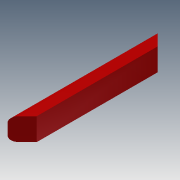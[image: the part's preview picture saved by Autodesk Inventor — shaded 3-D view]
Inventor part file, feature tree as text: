
AUTODESK INVENTOR PART (.ipt)
format: ipt  version: 2014 (Build 180170000, 170)  size: 93,184 bytes
history: native  units: in
note: dims shown in document units (in); Inventor stores cm internally (conversion verified against a paired STEP export)
features: extrude x2, sketch x2
ambient origin geometry x8: Origin, YZ Plane, XZ Plane, XY Plane, X Axis, Y Axis, Z Axis, Center Point
bodies: Solid1 (feature_tree)
feature tree (4):
  extrude  "Extrusion1"  Depth=5.0in
  extrude  "Extrusion2"  Depth=5.0in
  sketch  "Sketch1"  dims[d0=0.75in d1=5.0in]
  sketch  "Sketch2"  dims[d2=2.5in d3=2.5in d4=1.25in d5=33.5in d6=0.0in d8=45.0deg d10=45.0deg d11=5.0in d12=0.0in]
